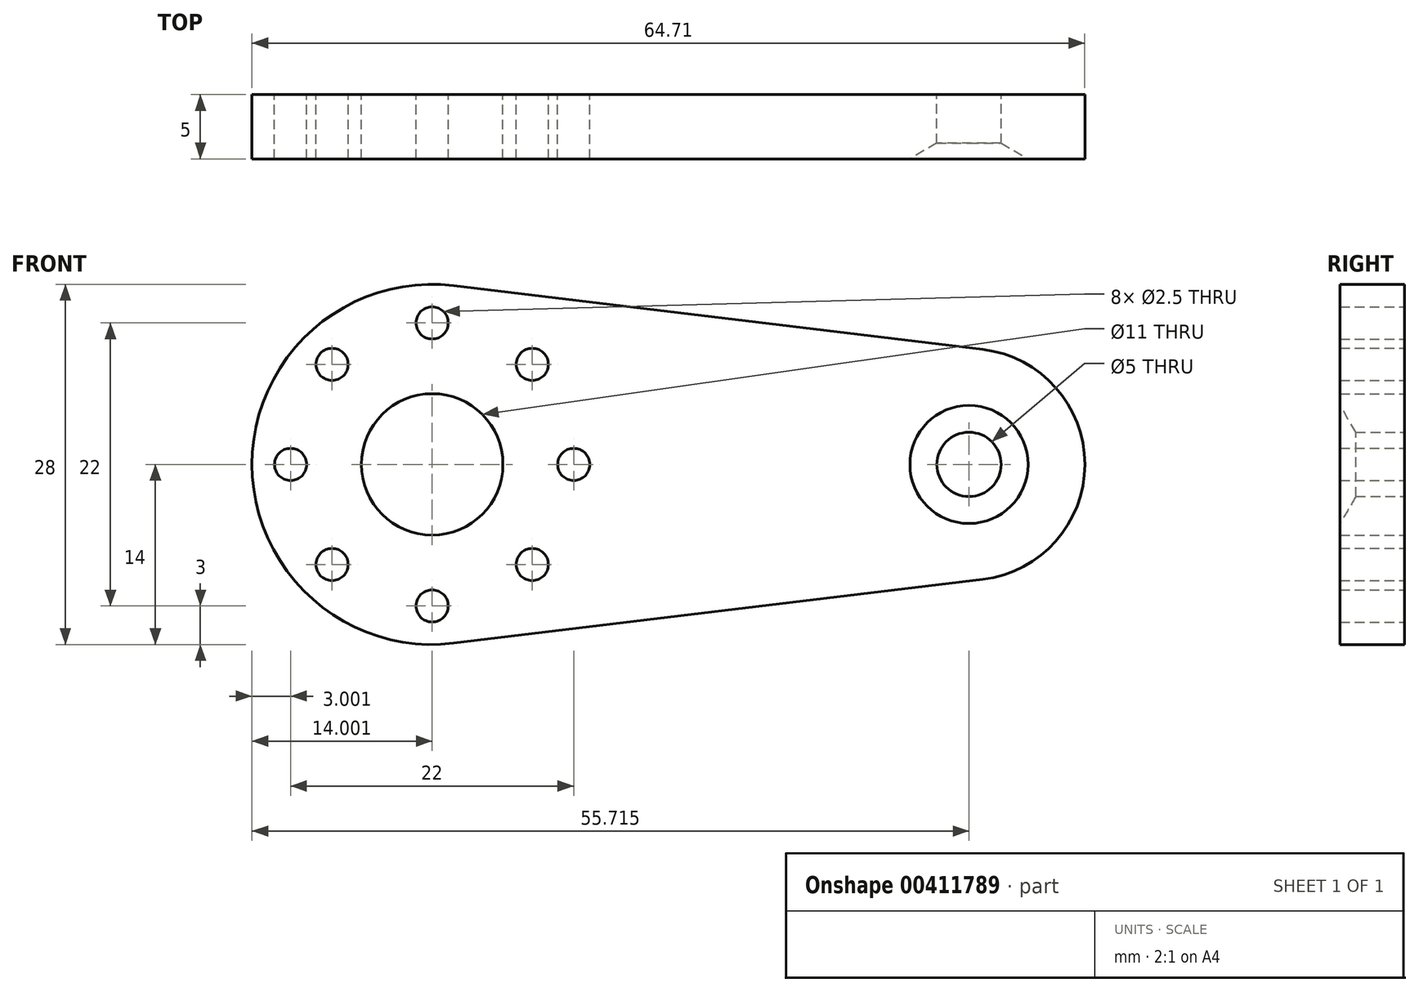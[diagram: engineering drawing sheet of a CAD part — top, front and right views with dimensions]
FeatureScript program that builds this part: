
annotation { "Feature Type Name" : "Feature", "Feature Type Description" : "" }
export const myFeature = defineFeature(function(context is Context, id is Id, definition is map)
    precondition{}
    {
        {
            var Q0;
            Q0=qCreatedBy(makeId("Front.planeOp"),FACE);
            var sketch = newSketch(context, id + "F0", { "sketchPlane" : qUnion([Q0])});
            skArc(sketch, "E0", {"start": v(-21.02, 13.9) * mm, "mid": v(-36.7, 0) * mm, "end": v(-21.02, -13.9) * mm});
            skArc(sketch, "E1", {"start": v(20.1, -8.94) * mm, "mid": v(28.01, 0) * mm, "end": v(20.1, 8.94) * mm});
            skLineSegment(sketch, "E2", {"start": v(-21.02, 13.9) * mm, "end": v(20.1, 8.94) * mm});
            skLineSegment(sketch, "E3", {"start": v(-21.02, -13.9) * mm, "end": v(20.1, -8.94) * mm});
            skCircle(sketch, "E4", {"center": v(19.01, 0) * mm, "radius": 2.5 * mm});
            skCircle(sketch, "E5", {"center": v(-22.7, 0) * mm, "radius": 5.5 * mm});
            skCircle(sketch, "E6", {"center": v(-33.7, 0) * mm, "radius": 1.25 * mm});
            skCircle(sketch, "E7.1.0", {"center": v(-30.48, -7.78) * mm, "radius": 1.25 * mm});
            skCircle(sketch, "E7.2.0", {"center": v(-22.7, -11) * mm, "radius": 1.25 * mm});
            skCircle(sketch, "E7.3.0", {"center": v(-14.92, -7.78) * mm, "radius": 1.25 * mm});
            skCircle(sketch, "E7.4.0", {"center": v(-11.7, 0) * mm, "radius": 1.25 * mm});
            skCircle(sketch, "E7.5.0", {"center": v(-14.92, 7.78) * mm, "radius": 1.25 * mm});
            skCircle(sketch, "E7.6.0", {"center": v(-22.7, 11) * mm, "radius": 1.25 * mm});
            skCircle(sketch, "E7.7.0", {"center": v(-30.48, 7.78) * mm, "radius": 1.25 * mm});
            skSolve(sketch);
        }
        {
            var Q0;
            Q0=qSketchRegion(id+"F0",true);
            extrude(context, id + "F1", {"entities" : qUnion([Q0]), "depth" : 5 * mm});
        }
        {
            var Q0;
            Q0=makeQuery(id+"F1.opExtrude","CAP_EDGE",EDGE,{"disambiguationData":[OSD([sQuery(id+"F0.wireOp",EDGE,"E4")])],"isStart":false});
            chamfer(context, id + "F2", {"entities" : qUnion([Q0]), "chamferType" : ChamferType.TWO_OFFSETS, "width1" : 1.22 * mm, "oppositeDirection" : false, "width2" : 2.09 * mm, "tangentPropagation" : true});
        }
    });
